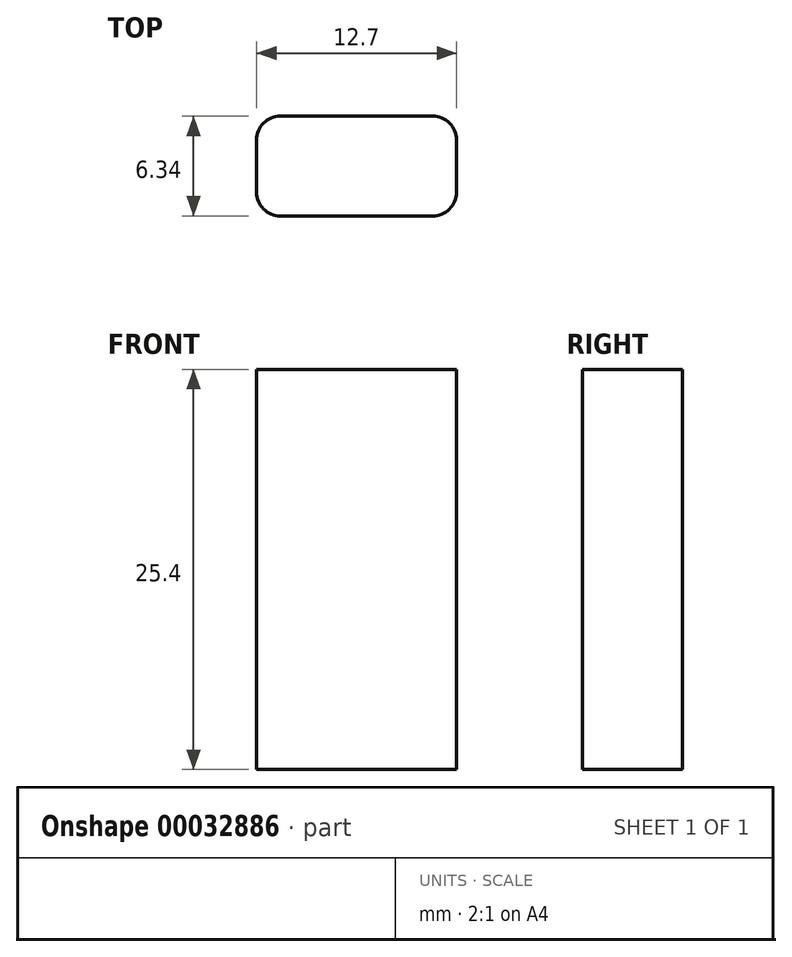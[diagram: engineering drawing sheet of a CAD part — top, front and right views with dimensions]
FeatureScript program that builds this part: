
annotation { "Feature Type Name" : "Feature", "Feature Type Description" : "" }
export const myFeature = defineFeature(function(context is Context, id is Id, definition is map)
    precondition{}
    {
        {
            var Q0;
            Q0=qCreatedBy(makeId("Top.planeOp"),FACE);
            var sketch = newSketch(context, id + "F0", { "sketchPlane" : qUnion([Q0])});
            skLineSegment(sketch, "E0.rect.bottom", {"start": v(-4.83, -3.18) * mm, "end": v(4.83, -3.18) * mm});
            skLineSegment(sketch, "E0.rect.top", {"start": v(-4.83, 3.18) * mm, "end": v(4.83, 3.18) * mm});
            skLineSegment(sketch, "E0.rect.left", {"start": v(-6.35, -1.65) * mm, "end": v(-6.35, 1.65) * mm});
            skLineSegment(sketch, "E0.rect.right", {"start": v(6.35, -1.65) * mm, "end": v(6.35, 1.65) * mm});
            skPoint(sketch, "E0.rect.middle", {"position": v(0, 0) * mm});
            skPoint(sketch, "E1.visualSharp", {"position": v(-6.35, 3.17) * mm});
            skArc(sketch, "E1.filletArc", {"start": v(-4.83, 3.17) * mm, "mid": v(-5.9, 2.73) * mm, "end": v(-6.35, 1.65) * mm});
            skPoint(sketch, "E2.visualSharp", {"position": v(6.35, 3.18) * mm});
            skArc(sketch, "E2.filletArc", {"start": v(6.35, 1.65) * mm, "mid": v(5.9, 2.73) * mm, "end": v(4.83, 3.18) * mm});
            skPoint(sketch, "E3.visualSharp", {"position": v(-6.35, -3.18) * mm});
            skArc(sketch, "E3.filletArc", {"start": v(-6.35, -1.65) * mm, "mid": v(-5.9, -2.73) * mm, "end": v(-4.83, -3.18) * mm});
            skPoint(sketch, "E4.visualSharp", {"position": v(6.35, -3.18) * mm});
            skArc(sketch, "E4.filletArc", {"start": v(4.83, -3.18) * mm, "mid": v(5.9, -2.73) * mm, "end": v(6.35, -1.65) * mm});
            skSolve(sketch);
        }
        {
            var Q0;
            Q0=makeQuery(id+"F0.imprint","IMPRINT",FACE,{"disambiguationData":[TD([[makeQuery(id+"F0.imprint","IMPRINT",EDGE,{"derivedFrom":sQuery(id+"F0.wireOp",EDGE,"E0.rect.bottom")}),1.0]])]});
            extrude(context, id + "F1", {"entities" : qUnion([Q0]), "depth" : 25.4 * mm});
        }
    });
